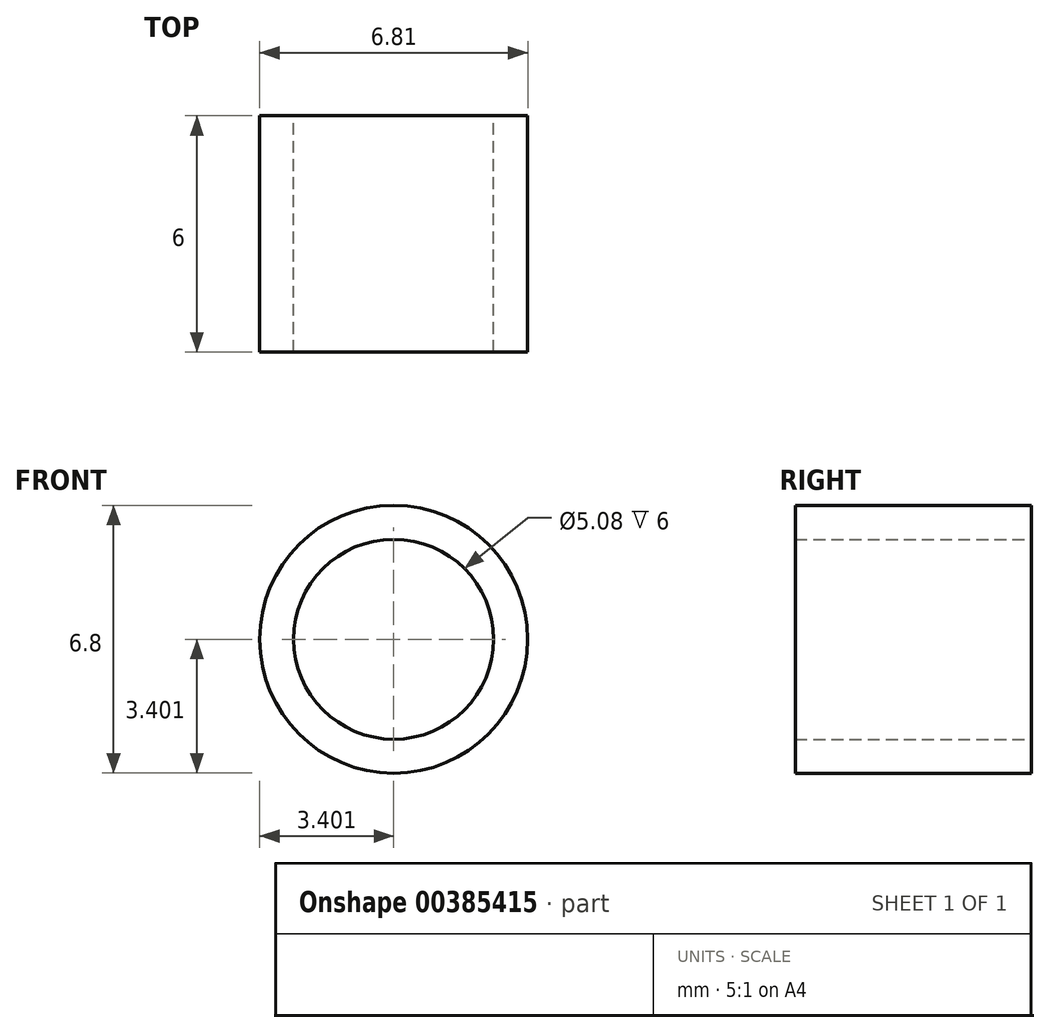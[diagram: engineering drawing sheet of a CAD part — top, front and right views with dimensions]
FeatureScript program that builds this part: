
annotation { "Feature Type Name" : "Feature", "Feature Type Description" : "" }
export const myFeature = defineFeature(function(context is Context, id is Id, definition is map)
    precondition{}
    {
        {
            var Q0;
            Q0=qCreatedBy(makeId("Front.planeOp"),FACE);
            var sketch = newSketch(context, id + "F0", { "sketchPlane" : qUnion([Q0])});
            skCircle(sketch, "E0", {"center": v(1.44, 26.28) * mm, "radius": 2.54 * mm});
            skCircle(sketch, "E1", {"center": v(1.44, 26.28) * mm, "radius": 3.4 * mm});
            skSolve(sketch);
        }
        {
            var Q0;
            Q0=qSketchRegion(id+"F0",true);
            extrude(context, id + "F1", {"entities" : qUnion([Q0]), "depth" : 6 * mm});
        }
    });
